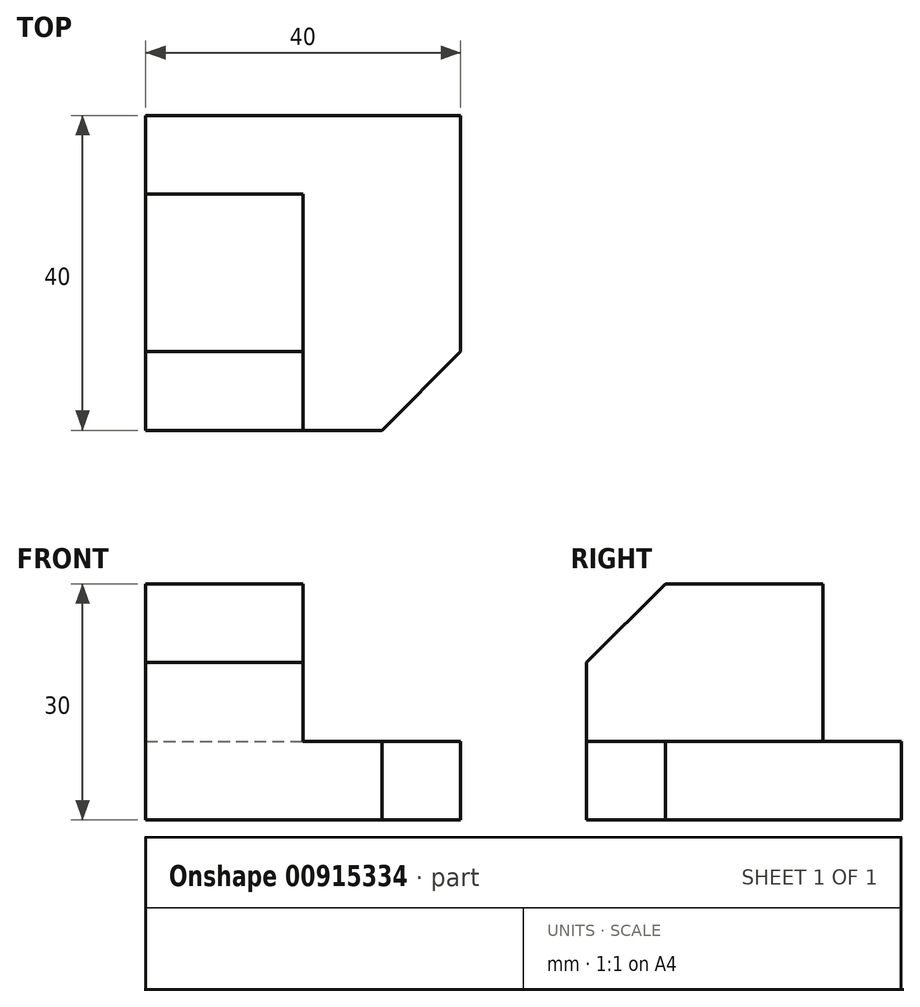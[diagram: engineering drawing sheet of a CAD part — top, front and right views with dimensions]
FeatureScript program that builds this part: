
annotation { "Feature Type Name" : "Feature", "Feature Type Description" : "" }
export const myFeature = defineFeature(function(context is Context, id is Id, definition is map)
    precondition{}
    {
        {
            var Q0;
            Q0=qCreatedBy(makeId("Top.planeOp"),FACE);
            var sketch = newSketch(context, id + "F0", { "sketchPlane" : qUnion([Q0])});
            skLineSegment(sketch, "E0.bottom", {"start": v(0, 0) * mm, "end": v(30, 0) * mm});
            skLineSegment(sketch, "E0.top", {"start": v(0, 40) * mm, "end": v(40, 40) * mm});
            skLineSegment(sketch, "E0.left", {"start": v(0, 0) * mm, "end": v(0, 40) * mm});
            skLineSegment(sketch, "E0.right", {"start": v(40, 10) * mm, "end": v(40, 40) * mm});
            skLineSegment(sketch, "E1", {"start": v(0, 30) * mm, "end": v(20, 30) * mm});
            skLineSegment(sketch, "E2", {"start": v(20, 30) * mm, "end": v(20, 0) * mm});
            skLineSegment(sketch, "E3", {"start": v(30, 0) * mm, "end": v(40, 10) * mm});
            skSolve(sketch);
        }
        {
            var Q0;
            {var subQ4=sQuery(id+"F0.wireOp",EDGE,"E1");Q0=makeQuery(id+"F0.imprint","IMPRINT",FACE,{"disambiguationData":[TD([[makeQuery(id+"F0.imprint","IMPRINT",EDGE,{"derivedFrom":subQ4}),-1.0]])]});}
            extrude(context, id + "F1", {"entities" : qUnion([Q0]), "depth" : 30 * mm, "offsetDistance" : 25 * mm});
        }
        {
            var Q0;
            {var subQ1=sQuery(id+"F0.wireOp",EDGE,"E0.top");Q0=makeQuery(id+"F0.imprint","IMPRINT",FACE,{"disambiguationData":[TD([[makeQuery(id+"F0.imprint","IMPRINT",EDGE,{"derivedFrom":subQ1}),-1.0]])]});}
            extrude(context, id + "F2", {"entities" : qUnion([Q0]), "operationType" : NewBodyOperationType.ADD, "depth" : 10 * mm, "offsetDistance" : 25 * mm});
        }
        {
            var Q0;
            Q0=makeQuery(id+"F1.opExtrude","CAP_EDGE",EDGE,{"disambiguationData":[OSD([sQuery(id+"F0.wireOp",EDGE,"E0.bottom")])],"isStart":false});
            chamfer(context, id + "F3", {"entities" : qUnion([Q0]), "width" : 10 * mm, "tangentPropagation" : true});
        }
    });
